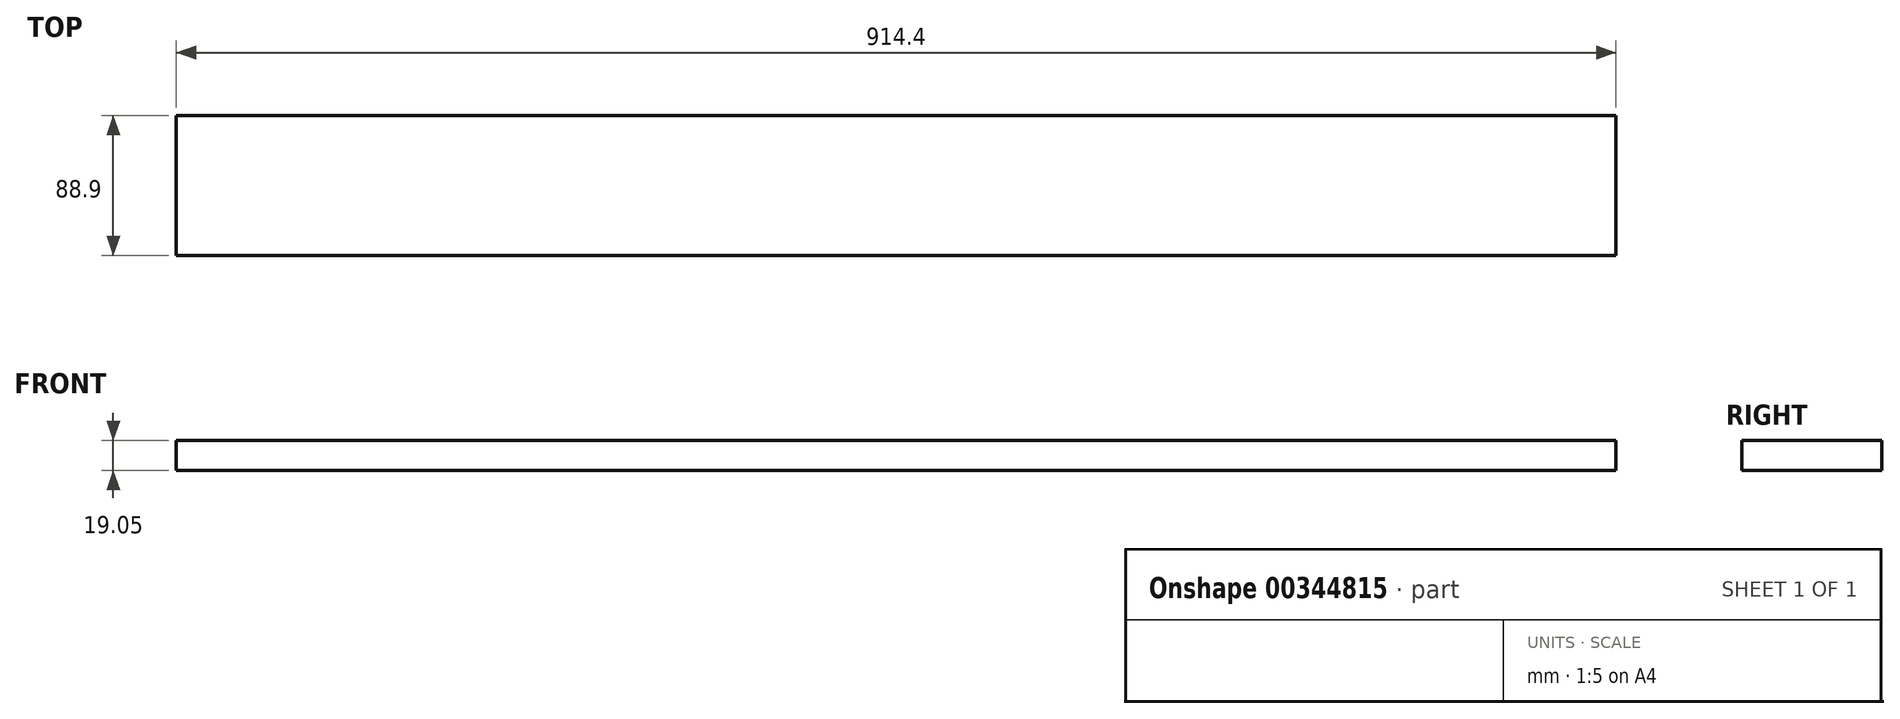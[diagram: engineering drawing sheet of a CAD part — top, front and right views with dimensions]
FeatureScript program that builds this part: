
annotation { "Feature Type Name" : "Feature", "Feature Type Description" : "" }
export const myFeature = defineFeature(function(context is Context, id is Id, definition is map)
    precondition{}
    {
        {
            var Q0;
            Q0=qCreatedBy(makeId("Right.planeOp"),FACE);
            var sketch = newSketch(context, id + "F0", { "sketchPlane" : qUnion([Q0])});
            skLineSegment(sketch, "E0.bottom", {"start": v(0, 0) * mm, "end": v(88.9, 0) * mm});
            skLineSegment(sketch, "E0.top", {"start": v(0, 19.05) * mm, "end": v(88.9, 19.05) * mm});
            skLineSegment(sketch, "E0.left", {"start": v(0, 0) * mm, "end": v(0, 19.05) * mm});
            skLineSegment(sketch, "E0.right", {"start": v(88.9, 0) * mm, "end": v(88.9, 19.05) * mm});
            skSolve(sketch);
        }
        {
            var Q0;
            Q0=makeQuery(id+"F0.imprint","IMPRINT",FACE,{"disambiguationData":[TD([[makeQuery(id+"F0.imprint","IMPRINT",EDGE,{"derivedFrom":sQuery(id+"F0.wireOp",EDGE,"E0.bottom")}),1.0]])]});
            extrude(context, id + "F1", {"entities" : qUnion([Q0]), "depth" : 914.4 * mm, "offsetDistance" : 25.4 * mm});
        }
    });
